# Revit family: Shower-Handshower-KOHLER-AWAKEN-K-72421T_1
name_source: partatom
category: Plumbing Fixtures
units: mm (PartAtom-declared; Revit-internal decimal feet)

## family parameters
Cut with Voids When Loaded = No
Host = Face
OmniClass Number = 23.31.17.00
OmniClass Title = Showers
Part Type = Normal
Room Calculation Point = No
Round Connector Dimension = Use Diameter
Shared = No

## types (4) — shared parameters
ADA Compliant = No
Assembly Code = D2010700
CW Connection = No
Cold Water Inlet = Cold Water Inlet
Date Modified = 11/23/2022
Default Elevation = 42"
Description = AWAKEN MULTI FUNCTION HAND SHOWER (ORG)
Drain Included = No
Flow Rate = 0 GPM
HW Connection = Yes
Height = 10 1/2"
Hot Water Inlet = Hot Water Inlet
Length = 3 3/4"
Manufacturer = Kohler Co.
Master Format 2014 = 22 42 23
Master Format 2014 Name = Residential Showers
Material = Plastic
Pressure = 0.00 psi
Product Name = AWAKEN
Tempered Water Inlet = Tempered Water Inlet
URL = http://www.kohler.com.cn
Vent Connection = No
Waste Connection = No
Waste Water Outlet = Waste Water Outlet
WaterSense Certified = No
Width = 4 5/8"

## per-type parameters (varying)
| type | Finish | Model | Secondary Finish | Type |
| BL-Matte Black | Kohler-Metal-BL-Matte_Black | K-72421T-BL | Kohler-Plastic-7-Black_Black | 3 |
| 2BL-Black | Kohler-Plastic-2BL-Black | K-72421T-2BL | Kohler-Plastic-7-Black_Black | 1 |
| AF-Vibrant French Gold | KOHLER-Plastic-AF-Vibrant_French_Gold | K-72421T-AF | Kohler-Plastic-0-White | 2 |
| BN-Brushed Nickel | KOHLER-Plastic-BN-Vibrant_Brushed_Nickel | K-72421T-BN | Kohler-Plastic-0-White | 4 |

## geometry (parser evidence)
native form markers: Sweep x4
no freeform markers — native parametric forms only
